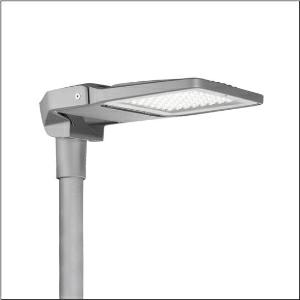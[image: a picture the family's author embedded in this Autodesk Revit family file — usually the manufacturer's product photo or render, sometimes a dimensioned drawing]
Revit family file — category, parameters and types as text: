
# Revit family: floodlight_fl_20_mini___pl52_5xa7672c2d4ac_d368
name_source: partatom
category: Lighting Fixtures
units: mm (PartAtom-declared; Revit-internal decimal feet)

## family parameters
Cut with Voids When Loaded = No
Host = Face
Light Source = No
Part Type = Normal
Room Calculation Point = No
Round Connector Dimension = Use Diameter
Shared = No

## types (1)
- --- (1 x LED 4000K / CRI = 70 (unbekannt), 12290 lm, 4000K)
    Apparent Load = 96 VA
    CIE Flux Codes = 27 59 98 100 100
    Color Rendering = 70
    Color Temperature = 4000K
    Default Elevation = 1800 mm
    Description = Floodlight FL 20 mini, floodlight, primary light control with lens, of plastic, primary optical cover: protective disc, of toughened safety glass, transparent, light distribution: PL52, light emission: direct distribution, primary light characteristic: asymmetric, installation type: side-entry, post-top, LED, High Power LED, rated luminous flux: 12.290lm, luminous efficacy: 128lm/W, light colour: 740, colour temperature: 4000K, control gear: ECG Plus, control: flexible luminous flux parameterisation, time-dependent luminous flux control, digital communication interface, overheat protection, power reduction, electronic power reduction, with terminal, 5-pole, max. 2.5mm², mains connection: 220..240V, AC, 50/60Hz, rated input power: 96W, LED unit, of diecast aluminium, powder-coated, Siteco® metallic grey (DB 702S), corrosivity category C5 mid according to DIN EN ISO 12944, incl. 1x M20 cable gland for cable Ø 6.5..12mm, inclination adjustable: 0°, 5°, 10°, 15°, please order mast flange separately, length: 565mm, width: 335mm, height: 119mm, housing frame, of diecast aluminium, powder-coated, Siteco® metallic grey (DB 702S), mast flange adapter, of diecast aluminium, powder-coated, Siteco® metallic grey (DB 702S), DALI, protection rating (complete): IP66, insulation class (complete): insulation class II (safety insulation), certification: CE, ENEC, VDE, protection symbol: D, permissible operating ambient temperature: -40..+40°C, permissible operating ambient temperature for outdoor applications: -40..+50°C, standard: DIN EN 12944, packaging unit: 1 piece

Light Distribution: PL52
    Height = 62 mm  [stored 0.203412 ft]
    Lamp = 1 x LED 4000K / CRI >= 70 (unbekannt)
    Lamp Light Flux = 12290 lm
    Lamp count = 1
    Length = 565 mm
    Luminous efficacy = 128 lm/W
    Manufacturer = Siteco
    ModVariant = No
    Model = 5XA7672C2D4AC
    Number of Poles = 1
    OnlyDefault = Yes
    Power Factor = 1
    Product Name = Floodlight FL 20 mini | PL52
    Product group = floodlight | pylon top
    ProductGroupID = 6101
    Protection Class = Protection class II
    Protection Degree = IP 66
    RLX_Detail_Level = 1
    RLX_Emergency_Light_Flux = 0 lm
    RLX_Emergency_Type = 0
    RLX_Emergency_Type_DB = No
    RlxData = <blob elided: 102133 chars, md5=3694e87b>
    Socket = socket
    Standby Power = 0 W
    System Light Flux = 12290 lm
    System Power = 96 W
    Type Comments = factory setting: luminous flux: 100 % | dim-lin: 254 | 500 mA
    Type Image = l_1005946.jpg
    URL = http://relux.com
    VarID = @adj_163597
    Voltage = 0 V
    Weight = 0.00 kg
    Width = 335 mm

note: [stored X ft] marks values corroborated as IEEE doubles in the binary element streams (Revit-internal decimal feet)

## geometry (parser evidence)
native form markers: Blend x4, Sweep x11
no freeform markers — native parametric forms only
